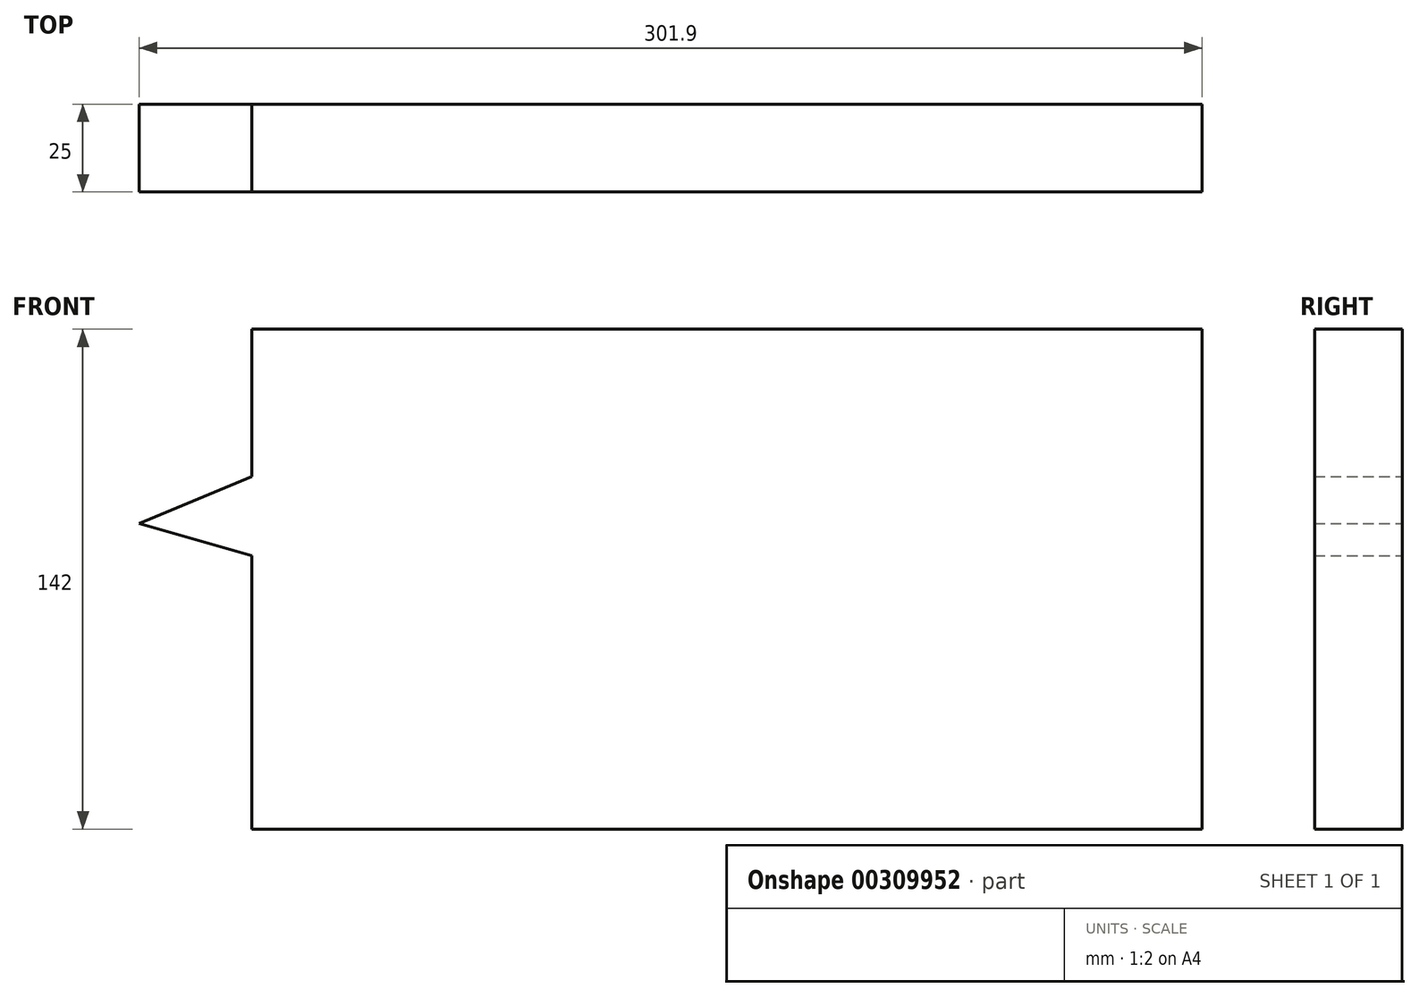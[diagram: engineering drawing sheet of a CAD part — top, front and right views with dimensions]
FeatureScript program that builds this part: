
annotation { "Feature Type Name" : "Feature", "Feature Type Description" : "" }
export const myFeature = defineFeature(function(context is Context, id is Id, definition is map)
    precondition{}
    {
        {
            var Q0;
            Q0=qCreatedBy(makeId("Front.planeOp"),FACE);
            var sketch = newSketch(context, id + "F0", { "sketchPlane" : qUnion([Q0])});
            skLineSegment(sketch, "E0.bottom", {"start": v(-97.38, 65) * mm, "end": v(172.62, 65) * mm});
            skLineSegment(sketch, "E0.top", {"start": v(-97.38, -77) * mm, "end": v(172.62, -77) * mm});
            skLineSegment(sketch, "E0.left", {"start": v(-97.38, 65) * mm, "end": v(-97.38, -77) * mm});
            skLineSegment(sketch, "E0.right", {"start": v(172.62, 65) * mm, "end": v(172.62, -77) * mm});
            skLineSegment(sketch, "E1", {"start": v(-253.61, -42.53) * mm, "end": v(-35.38, 49.25) * mm});
            skLineSegment(sketch, "E2", {"start": v(-35.38, 49.25) * mm, "end": v(-20.42, -21.46) * mm});
            skLineSegment(sketch, "E3", {"start": v(-20.42, -21.46) * mm, "end": v(-129.28, 9.76) * mm});
            skSolve(sketch);
        }
        {
            var Q0;
            Q0 = qSketchRegion(id + "F0", true);
            extrude(context, id + "F1", {"entities" : qUnion([Q0]), "depth" : 25 * mm});
        }
    });
